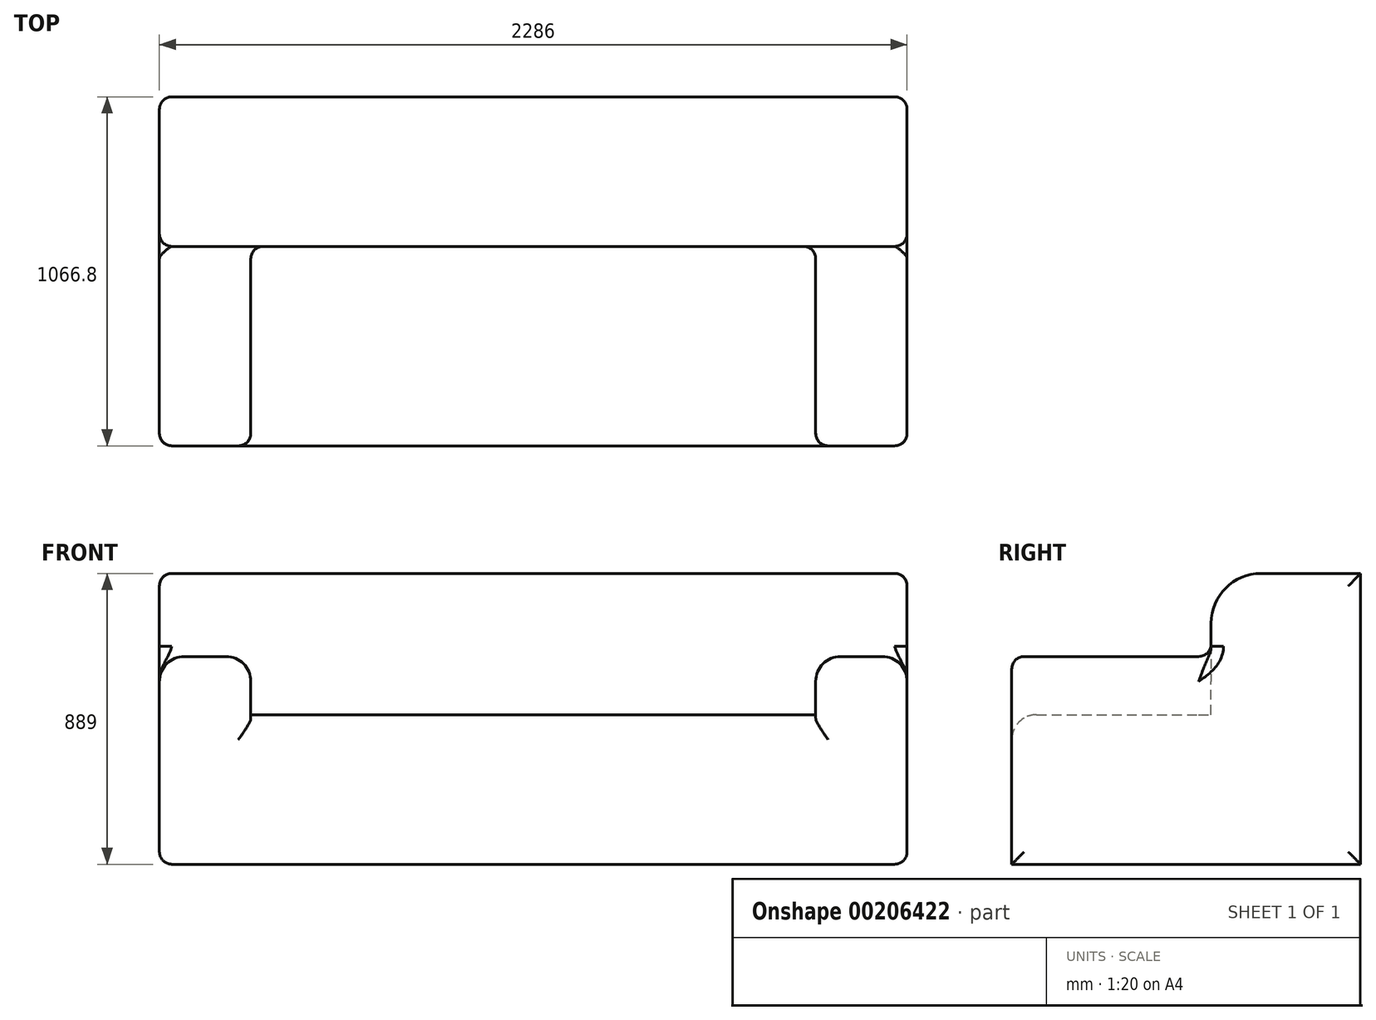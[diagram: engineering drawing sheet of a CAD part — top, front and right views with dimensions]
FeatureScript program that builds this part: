
annotation { "Feature Type Name" : "Feature", "Feature Type Description" : "" }
export const myFeature = defineFeature(function(context is Context, id is Id, definition is map)
    precondition{}
    {
        {
            var Q0;
            Q0=qCreatedBy(makeId("Front.planeOp"),FACE);
            var sketch = newSketch(context, id + "F0", { "sketchPlane" : qUnion([Q0])});
            skLineSegment(sketch, "E0.bottom", {"start": v(0, 0) * mm, "end": v(-863.6, 0) * mm});
            skLineSegment(sketch, "E0.top", {"start": v(0, 457.2) * mm, "end": v(-863.6, 457.2) * mm});
            skLineSegment(sketch, "E0.left", {"start": v(0, 0) * mm, "end": v(0, 457.2) * mm});
            skLineSegment(sketch, "E0.right", {"start": v(-863.6, 0) * mm, "end": v(-863.6, 457.2) * mm});
            skSolve(sketch);
        }
        {
            var Q0;
            Q0=makeQuery(id+"F0.imprint","IMPRINT",FACE,{"disambiguationData":[TD([[makeQuery(id+"F0.imprint","IMPRINT",EDGE,{"derivedFrom":sQuery(id+"F0.wireOp",EDGE,"E0.bottom")}),-1.0]])]});
            extrude(context, id + "F1", {"entities" : qUnion([Q0]), "depth" : 609.6 * mm});
        }
        {
            var Q0;
            Q0=makeQuery(id+"F1.opExtrude","CAP_FACE",FACE,{"disambiguationData":[OSD([sQuery(id+"F0.wireOp",EDGE,"E0.bottom"),sQuery(id+"F0.wireOp",EDGE,"E0.top"),sQuery(id+"F0.wireOp",EDGE,"E0.left"),sQuery(id+"F0.wireOp",EDGE,"E0.right")])],"isStart":false});
            var sketch = newSketch(context, id + "F2", { "sketchPlane" : qUnion([Q0])});
            skLineSegment(sketch, "E1.bottom", {"start": v(-863.6, 0) * mm, "end": v(-1143, 0) * mm});
            skLineSegment(sketch, "E1.top", {"start": v(-863.6, 635) * mm, "end": v(-1143, 635) * mm});
            skLineSegment(sketch, "E1.left", {"start": v(-863.6, 0) * mm, "end": v(-863.6, 635) * mm});
            skLineSegment(sketch, "E1.right", {"start": v(-1143, 0) * mm, "end": v(-1143, 635) * mm});
            skSolve(sketch);
        }
        {
            var Q0;
            {var subQ3=sQuery(id+"F2.wireOp",EDGE,"E1.bottom");Q0=makeQuery(id+"F2.imprint","IMPRINT",FACE,{"disambiguationData":[TD([[makeQuery(id+"F2.imprint","IMPRINT",EDGE,{"derivedFrom":subQ3}),-1.0]])]});}
            extrude(context, id + "F3", {"entities" : qUnion([Q0]), "operationType" : NewBodyOperationType.ADD, "oppositeDirection" : true, "depth" : 609.6 * mm});
        }
        {
            var Q0;
            Q0=makeQuery(id+"F3.boolean.opBoolean","MERGE",FACE,{"derivedFrom":[makeQuery(id+"F1.opExtrude","CAP_FACE",FACE,{"disambiguationData":[OSD([sQuery(id+"F0.wireOp",EDGE,"E0.bottom"),sQuery(id+"F0.wireOp",EDGE,"E0.top"),sQuery(id+"F0.wireOp",EDGE,"E0.left"),sQuery(id+"F0.wireOp",EDGE,"E0.right")])],"isStart":true}),makeQuery(id+"F3.opExtrude","CAP_FACE",FACE,{"disambiguationData":[OSD([sQuery(id+"F2.wireOp",EDGE,"E1.bottom"),sQuery(id+"F2.wireOp",EDGE,"E1.top"),sQuery(id+"F2.wireOp",EDGE,"E1.left"),sQuery(id+"F2.wireOp",EDGE,"E1.right")])],"isStart":false})]});
            var sketch = newSketch(context, id + "F4", { "sketchPlane" : qUnion([Q0])});
            skLineSegment(sketch, "E2.bottom", {"start": v(1143, 0) * mm, "end": v(0, 0) * mm});
            skLineSegment(sketch, "E2.top", {"start": v(1143, 889) * mm, "end": v(0, 889) * mm});
            skLineSegment(sketch, "E2.left", {"start": v(1143, 0) * mm, "end": v(1143, 889) * mm});
            skLineSegment(sketch, "E2.right", {"start": v(0, 0) * mm, "end": v(0, 889) * mm});
            skSolve(sketch);
        }
        {
            var Q0;
            Q0 = qSketchRegion(id + "F4", true);
            extrude(context, id + "F5", {"entities" : qUnion([Q0]), "operationType" : NewBodyOperationType.ADD, "depth" : 457.2 * mm});
        }
        {
            var Q0;
            Q0=makeQuery(id+"F3.opExtrude","SWEPT_EDGE",EDGE,{"disambiguationData":[OSD([sQuery(id+"F2.wireOp",EDGE,"E1.top"),sQuery(id+"F2.wireOp",EDGE,"E1.right")])]});
            var Q1;
            Q1=makeQuery(id+"F3.opExtrude","SWEPT_EDGE",EDGE,{"disambiguationData":[OSD([sQuery(id+"F2.wireOp",EDGE,"E1.top"),sQuery(id+"F2.wireOp",EDGE,"E1.left")])]});
            fillet(context, id + "F6", {"entities" : qUnion([Q0, Q1]), "radius" : 76.2 * mm, "tangentPropagation" : true, "allowEdgeOverflow" : false});
        }
        {
            var Q0;
            Q0=makeQuery(id+"F6.opFillet","BLEND_EDGE",EDGE,{"blendedFrom":[makeQuery(id+"F3.opExtrude","SWEPT_EDGE",EDGE,{"disambiguationData":[OSD([sQuery(id+"F2.wireOp",EDGE,"E1.top"),sQuery(id+"F2.wireOp",EDGE,"E1.right")])]}),makeQuery(id+"F5.opExtrude","CAP_FACE",FACE,{"disambiguationData":[OSD([sQuery(id+"F4.wireOp",EDGE,"E2.bottom"),sQuery(id+"F4.wireOp",EDGE,"E2.top"),sQuery(id+"F4.wireOp",EDGE,"E2.left"),sQuery(id+"F4.wireOp",EDGE,"E2.right")])],"isStart":true})],"blendedInto":[makeQuery(id+"F5.opExtrude","CAP_FACE",FACE,{"disambiguationData":[OSD([sQuery(id+"F4.wireOp",EDGE,"E2.bottom"),sQuery(id+"F4.wireOp",EDGE,"E2.top"),sQuery(id+"F4.wireOp",EDGE,"E2.left"),sQuery(id+"F4.wireOp",EDGE,"E2.right")])],"isStart":true})]});
            var Q1;
            Q1=makeQuery(id+"F3.opExtrude","CAP_EDGE",EDGE,{"disambiguationData":[OSD([sQuery(id+"F2.wireOp",EDGE,"E1.top")])],"isStart":false});
            var Q2;
            Q2=makeQuery(id+"F6.opFillet","BLEND_EDGE",EDGE,{"blendedFrom":[makeQuery(id+"F3.opExtrude","SWEPT_EDGE",EDGE,{"disambiguationData":[OSD([sQuery(id+"F2.wireOp",EDGE,"E1.top"),sQuery(id+"F2.wireOp",EDGE,"E1.left")])]}),makeQuery(id+"F5.opExtrude","CAP_FACE",FACE,{"disambiguationData":[OSD([sQuery(id+"F4.wireOp",EDGE,"E2.bottom"),sQuery(id+"F4.wireOp",EDGE,"E2.top"),sQuery(id+"F4.wireOp",EDGE,"E2.left"),sQuery(id+"F4.wireOp",EDGE,"E2.right")])],"isStart":true})],"blendedInto":[makeQuery(id+"F5.opExtrude","CAP_FACE",FACE,{"disambiguationData":[OSD([sQuery(id+"F4.wireOp",EDGE,"E2.bottom"),sQuery(id+"F4.wireOp",EDGE,"E2.top"),sQuery(id+"F4.wireOp",EDGE,"E2.left"),sQuery(id+"F4.wireOp",EDGE,"E2.right")])],"isStart":true})]});
            var Q3;
            Q3=makeQuery(id+"F3.opExtrude","CAP_EDGE",EDGE,{"disambiguationData":[OSD([sQuery(id+"F2.wireOp",EDGE,"E1.left")])],"isStart":false});
            var Q4;
            Q4=makeQuery(id+"F1.opExtrude","CAP_EDGE",EDGE,{"disambiguationData":[OSD([sQuery(id+"F0.wireOp",EDGE,"E0.top")])],"isStart":true});
            fillet(context, id + "F7", {"entities" : qUnion([Q0, Q1, Q2, Q3, Q4]), "radius" : 38.1 * mm, "tangentPropagation" : true, "allowEdgeOverflow" : false});
        }
        {
            var Q0;
            Q0=makeQuery(id+"F5.boolean.opBoolean","MERGE",FACE,{"derivedFrom":[makeQuery(id+"F3.opExtrude","SWEPT_FACE",FACE,{"disambiguationData":[OSD([sQuery(id+"F2.wireOp",EDGE,"E1.right")])]}),makeQuery(id+"F5.opExtrude","SWEPT_FACE",FACE,{"disambiguationData":[OSD([sQuery(id+"F4.wireOp",EDGE,"E2.left")])]})]});
            fillet(context, id + "F8", {"entities" : qUnion([Q0]), "radius" : 38.1 * mm, "tangentPropagation" : true, "allowEdgeOverflow" : false});
        }
        {
            var Q0;
            Q0=makeQuery(id+"F5.opExtrude","CAP_EDGE",EDGE,{"disambiguationData":[OSD([sQuery(id+"F4.wireOp",EDGE,"E2.top")])],"isStart":true});
            fillet(context, id + "F9", {"entities" : qUnion([Q0]), "radius" : 152.4 * mm, "tangentPropagation" : true, "allowEdgeOverflow" : false});
        }
        {
            var Q0;
            Q0=makeQuery(id+"F1.opExtrude","CAP_EDGE",EDGE,{"disambiguationData":[OSD([sQuery(id+"F0.wireOp",EDGE,"E0.top")])],"isStart":false});
            fillet(context, id + "F10", {"entities" : qUnion([Q0]), "radius" : 76.2 * mm, "tangentPropagation" : true, "allowEdgeOverflow" : false});
        }
        {
            var Q0;
            Q0=makeQuery(id+"F1.opExtrude","SWEPT_BODY",BODY,{"disambiguationData":[OSD([sQuery(id+"F0.wireOp",EDGE,"E0.bottom"),sQuery(id+"F0.wireOp",EDGE,"E0.top"),sQuery(id+"F0.wireOp",EDGE,"E0.left"),sQuery(id+"F0.wireOp",EDGE,"E0.right")])]});
            var Q1;
            Q1=makeQuery(id+"F5.boolean.opBoolean","MERGE",FACE,{"derivedFrom":[makeQuery(id+"F1.opExtrude","SWEPT_FACE",FACE,{"disambiguationData":[OSD([sQuery(id+"F0.wireOp",EDGE,"E0.left")])]}),makeQuery(id+"F5.opExtrude","SWEPT_FACE",FACE,{"disambiguationData":[OSD([sQuery(id+"F4.wireOp",EDGE,"E2.right")])]})]});
            mirror(context, id + "F11", {"operationType" : NewBodyOperationType.ADD, "entities" : qUnion([Q0]), "mirrorPlane" : qUnion([Q1])});
        }
    });
